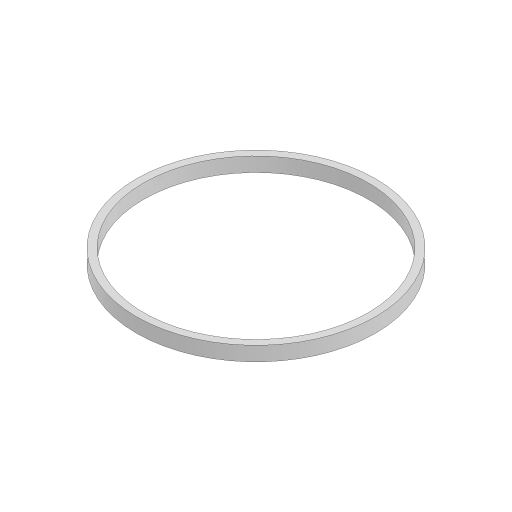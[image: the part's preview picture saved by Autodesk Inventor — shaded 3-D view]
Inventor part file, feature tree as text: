
AUTODESK INVENTOR PART (.ipt)
format: ipt  version: 2023 (Build 270158000, 158)  size: 89,088 bytes
history: native  units: in
note: dims shown in document units (in); Inventor stores cm internally (conversion verified against a paired STEP export)
features: extrude x1, sketch x1
ambient origin geometry x8: Origin, YZ Plane, XZ Plane, XY Plane, X Axis, Y Axis, Z Axis, Center Point
bodies: Solid1 (feature_tree)
feature tree (2):
  extrude  "Extrusion1"  Depth=236.2205in TaperAngle=0.0deg
  sketch  "Sketch1"  dims[d0=3937.0079in d1=236.2205in d2=0.0in]
